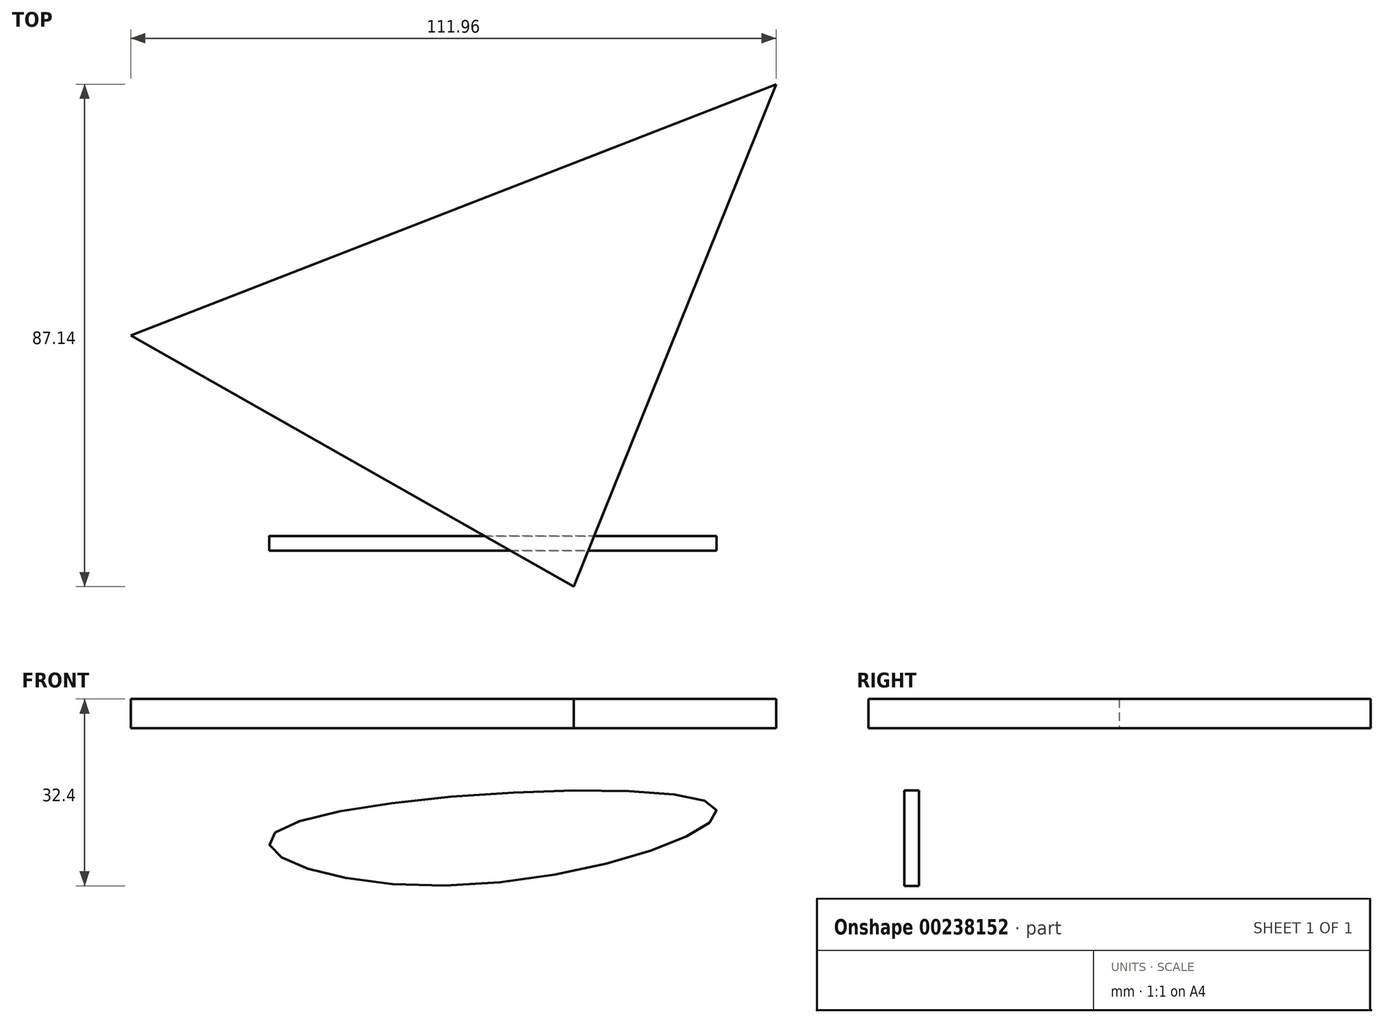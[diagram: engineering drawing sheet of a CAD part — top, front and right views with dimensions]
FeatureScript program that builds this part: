
annotation { "Feature Type Name" : "Feature", "Feature Type Description" : "" }
export const myFeature = defineFeature(function(context is Context, id is Id, definition is map)
    precondition{}
    {
        {
            var Q0;
            Q0=qCreatedBy(makeId("Top.planeOp"),FACE);
            var sketch = newSketch(context, id + "F0", { "sketchPlane" : qUnion([Q0])});
            skLineSegment(sketch, "E0", {"start": v(-153.96, 34.79) * mm, "end": v(-42, 78.38) * mm});
            skLineSegment(sketch, "E1", {"start": v(-42, 78.38) * mm, "end": v(-77.13, -8.76) * mm});
            skLineSegment(sketch, "E2", {"start": v(-77.13, -8.76) * mm, "end": v(-153.96, 34.79) * mm});
            skSolve(sketch);
        }
        {
            var Q0;
            Q0=makeQuery(id+"F0.imprint","IMPRINT",FACE,{"disambiguationData":[TD([[makeQuery(id+"F0.imprint","IMPRINT",EDGE,{"derivedFrom":sQuery(id+"F0.wireOp",EDGE,"E0")}),-1.0]])]});
            extrude(context, id + "F1", {"entities" : qUnion([Q0]), "depth" : 5.08 * mm});
        }
        {
            var Q0;
            Q0=qCreatedBy(makeId("Front.planeOp"),FACE);
            var sketch = newSketch(context, id + "F2", { "sketchPlane" : qUnion([Q0])});
            skFitSpline(sketch, "E3", {"points": [v(-128.92, -18.1) * mm, v(-53.09, -13.23) * mm, v(-98.59, -27.3) * mm, v(-128.92, -18.1) * mm]});
            skSolve(sketch);
        }
        {
            var Q0;
            Q0=makeQuery(id+"F2.imprint","IMPRINT",FACE,{"disambiguationData":[TD([[makeQuery(id+"F2.imprint","IMPRINT",EDGE,{"derivedFrom":sQuery(id+"F2.wireOp",EDGE,"E3")}),-1.0]])]});
            extrude(context, id + "F3", {"entities" : qUnion([Q0]), "depth" : 2.54 * mm});
        }
    });
